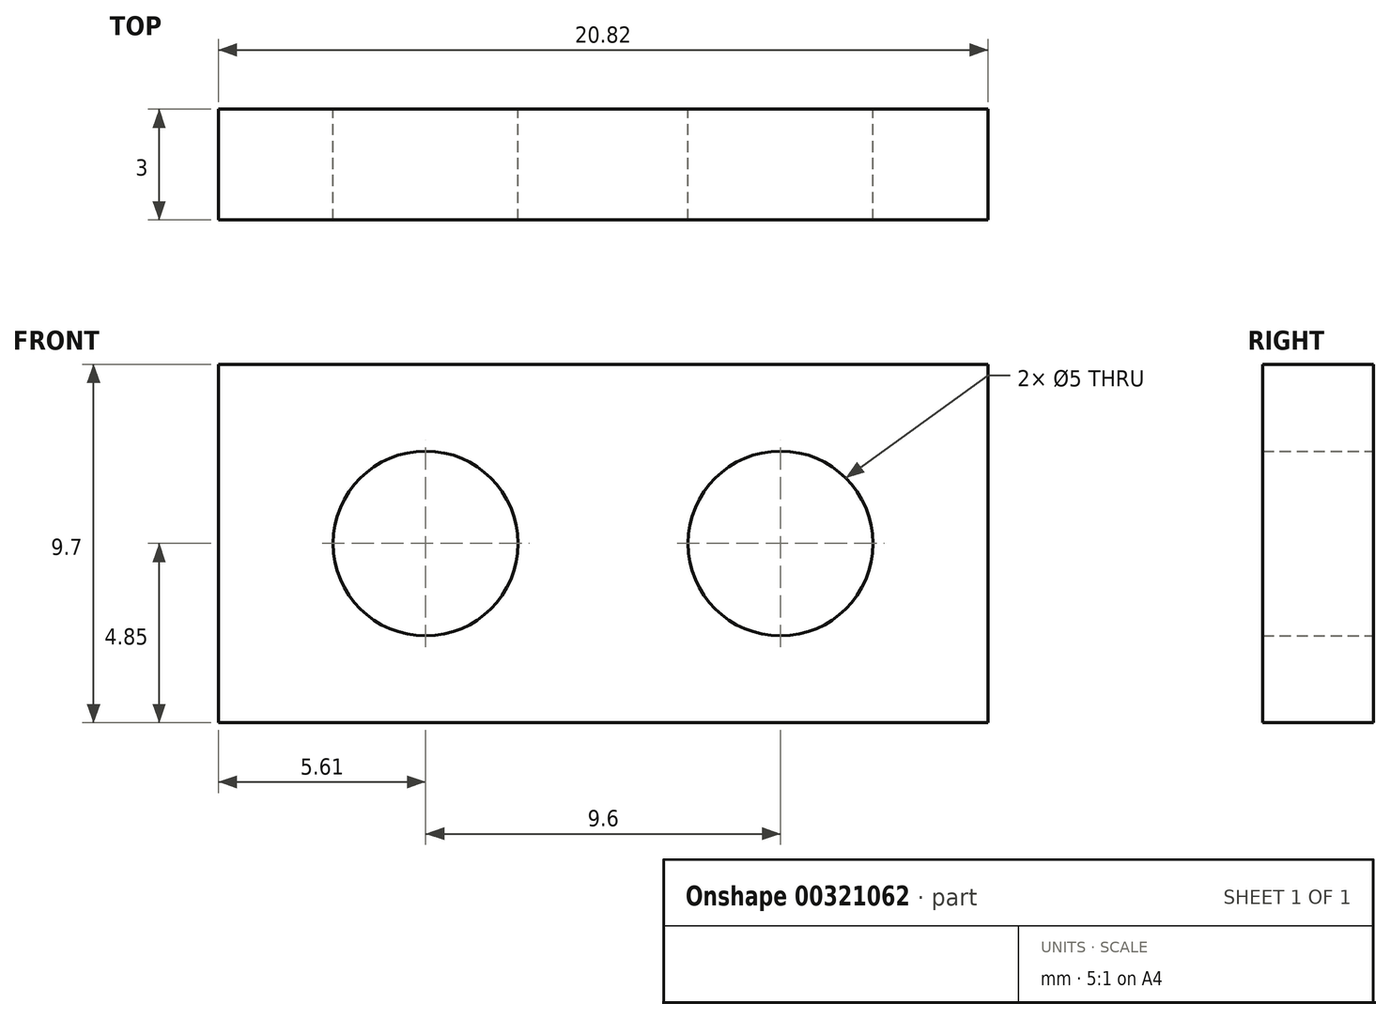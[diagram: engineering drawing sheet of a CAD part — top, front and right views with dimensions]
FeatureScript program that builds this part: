
annotation { "Feature Type Name" : "Feature", "Feature Type Description" : "" }
export const myFeature = defineFeature(function(context is Context, id is Id, definition is map)
    precondition{}
    {
        {
            var Q0;
            Q0=qCreatedBy(makeId("Front.planeOp"),FACE);
            var sketch = newSketch(context, id + "F0", { "sketchPlane" : qUnion([Q0])});
            skLineSegment(sketch, "E0.bottom", {"start": v(10.41, 4.85) * mm, "end": v(-10.41, 4.85) * mm});
            skLineSegment(sketch, "E0.top", {"start": v(10.41, -4.85) * mm, "end": v(-10.41, -4.85) * mm});
            skLineSegment(sketch, "E0.left", {"start": v(10.41, 4.85) * mm, "end": v(10.41, -4.85) * mm});
            skLineSegment(sketch, "E0.right", {"start": v(-10.41, 4.85) * mm, "end": v(-10.41, -4.85) * mm});
            skLineSegment(sketch, "E1.bottom", {"start": v(4.8, 0) * mm, "end": v(-4.8, 0) * mm, "construction": true});
            skLineSegment(sketch, "E1.top", {"start": v(4.8, 0) * mm, "end": v(-4.8, 0) * mm, "construction": true});
            skLineSegment(sketch, "E1.left", {"start": v(4.8, 0) * mm, "end": v(4.8, 0) * mm});
            skLineSegment(sketch, "E1.right", {"start": v(-4.8, 0) * mm, "end": v(-4.8, 0) * mm});
            skPoint(sketch, "E1.middle", {"position": v(0, 0) * mm});
            skCircle(sketch, "E2", {"center": v(-4.8, 0) * mm, "radius": 2.5 * mm});
            skCircle(sketch, "E3", {"center": v(4.8, 0) * mm, "radius": 2.5 * mm});
            skSolve(sketch);
        }
        {
            var Q0;
            Q0 = qSketchRegion(id + "F0", true);
            extrude(context, id + "F1", {"entities" : qUnion([Q0]), "depth" : 3 * mm});
        }
    });
